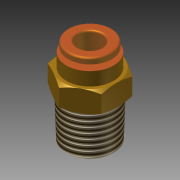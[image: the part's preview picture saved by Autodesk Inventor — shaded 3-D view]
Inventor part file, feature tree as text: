
AUTODESK INVENTOR PART (.ipt)
format: ipt  version: 2014 SP1 (Build 180222100, 222)  size: 172,032 bytes
history: native  units: mm
features: imported_body x1, thread x1
ambient origin geometry x8: Origin, YZ Plane, XZ Plane, XY Plane, X Axis, Y Axis, Z Axis, Center Point
bodies: Solid1 (feature_tree)
feature tree (2):
  imported_body  "Base1"
  thread  "Thread2"  [1 undecoded]
note: 1 required parameter value undecoded (feature->parameter linkage not recoverable at this tier; creation-order binding heuristic only, values carry confidence <= 0.55)
